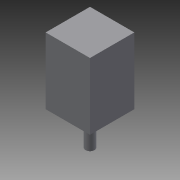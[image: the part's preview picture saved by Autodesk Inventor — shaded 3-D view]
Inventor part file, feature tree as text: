
AUTODESK INVENTOR PART (.ipt)
format: ipt  version: 2014 SP2 (Build 180246200, 246)  size: 102,912 bytes
history: native  units: mm
features: sketch x4, extrude x3, hole x1
ambient origin geometry x8: Origin, YZ Plane, XZ Plane, XY Plane, X Axis, Y Axis, Z Axis, Center Point
bodies: Solid1 (feature_tree)
feature tree (8):
  extrude  "Extrusion1"  Depth=20.0mm
  hole  "Hole1"  [1 undecoded]
  extrude  "Extrusion2"  Depth=8.0mm
  extrude  "Extrusion3"  Depth=13.5mm
  sketch  "Sketch1"  dims[d0=20.0mm d1=20.0mm]
  sketch  "Sketch2"  dims[d2=30.0mm d3=0.0mm d4=8.0mm]
  sketch  "Sketch3"  dims[d5=8.0mm d6=8.0mm]
  sketch  "Sketch4"  dims[d7=8.0mm d8=8.0mm d9=8.0mm d10=8.0mm d11=8.0mm d12=2.0mm d13=6.0mm d14=4.0mm d15=2.0mm d16=90.0deg d17=3.5mm d18=20.594885mm d19=15.0mm d20=1.5mm d21=0.0mm d22=4.0mm d23=13.5mm d24=0.0mm]
note: 1 required parameter value undecoded (feature->parameter linkage not recoverable at this tier; creation-order binding heuristic only, values carry confidence <= 0.55)
